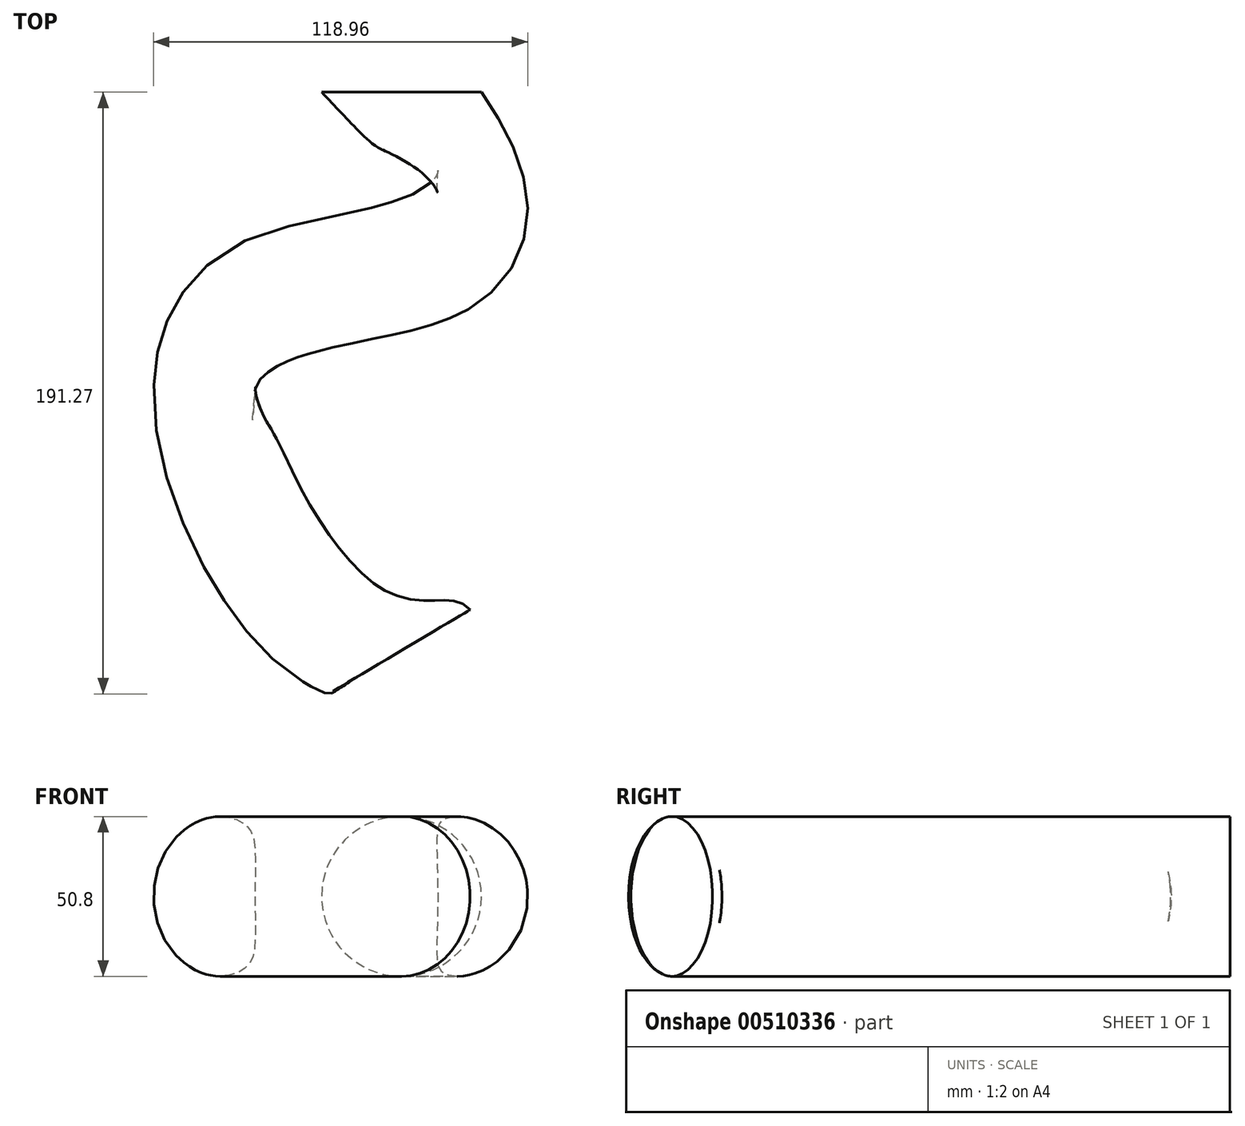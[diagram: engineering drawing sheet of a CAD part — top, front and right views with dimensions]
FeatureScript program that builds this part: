
annotation { "Feature Type Name" : "Feature", "Feature Type Description" : "" }
export const myFeature = defineFeature(function(context is Context, id is Id, definition is map)
    precondition{}
    {
        {
            var Q0;
            Q0=qCreatedBy(makeId("Front.planeOp"),FACE);
            var sketch = newSketch(context, id + "F0", { "sketchPlane" : qUnion([Q0])});
            skCircle(sketch, "E0", {"center": v(0, 0) * mm, "radius": 25.4 * mm});
            skSolve(sketch);
        }
        {
            var Q0;
            Q0=qCreatedBy(makeId("Top.planeOp"),FACE);
            var sketch = newSketch(context, id + "F1", { "sketchPlane" : qUnion([Q0])});
            skFitSpline(sketch, "E1", {"points": [v(0, 0) * mm, v(-44.97, -70.07) * mm, v(-29.48, -161.54) * mm, v(0, -177.48) * mm], "startDerivative": vector(406.23, -500.17) * mm, "endDerivative": vector(61.1, -22.47) * mm});
            skSolve(sketch);
        }
        {
            var Q0;
            Q0=makeQuery(id+"F0.imprint","IMPRINT",FACE,{"disambiguationData":[TD([[makeQuery(id+"F0.imprint","IMPRINT",EDGE,{"derivedFrom":sQuery(id+"F0.wireOp",EDGE,"E0")}),1.0]])]});
            var Q1;
            Q1=sQuery(id+"F1.wireOp",EDGE,"E1");
            sweep(context, id + "F2", {"profiles" : qUnion([Q0]), "path" : qUnion([Q1])});
        }
    });
